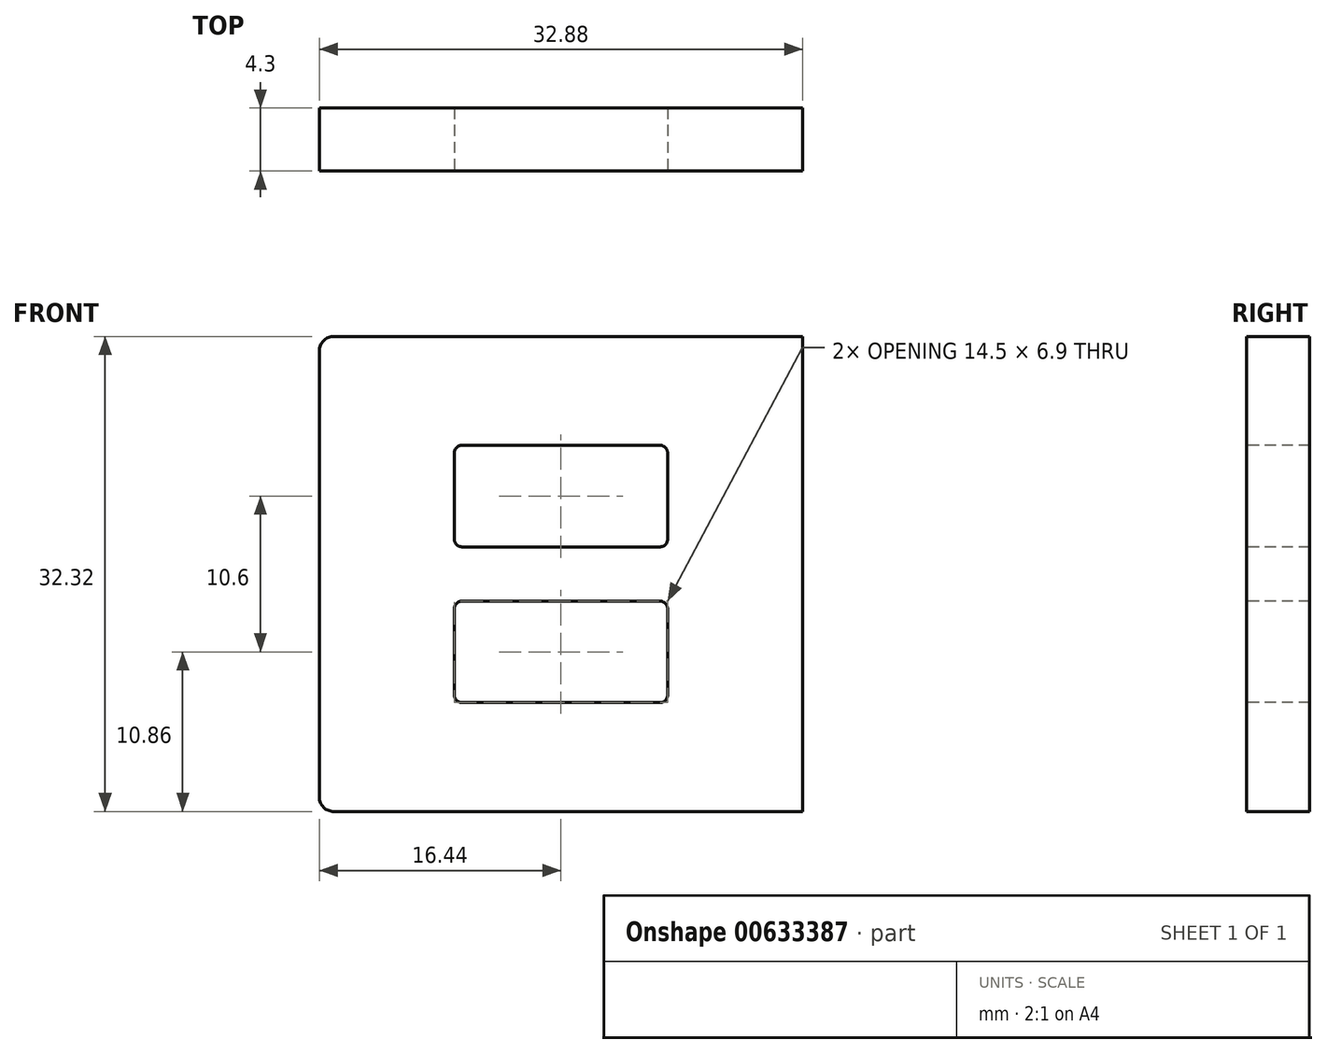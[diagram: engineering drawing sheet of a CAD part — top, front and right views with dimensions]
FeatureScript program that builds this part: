
annotation { "Feature Type Name" : "Feature", "Feature Type Description" : "" }
export const myFeature = defineFeature(function(context is Context, id is Id, definition is map)
    precondition{}
    {
        {
            var Q0;
            Q0=qCreatedBy(makeId("Front.planeOp"),FACE);
            var sketch = newSketch(context, id + "F0", { "sketchPlane" : qUnion([Q0])});
            skLineSegment(sketch, "E0.bottom", {"start": v(16.44, 16.16) * mm, "end": v(-15.44, 16.16) * mm});
            skLineSegment(sketch, "E0.top", {"start": v(16.44, -16.16) * mm, "end": v(-15.44, -16.16) * mm});
            skLineSegment(sketch, "E0.left", {"start": v(16.44, 16.16) * mm, "end": v(16.44, -16.16) * mm});
            skLineSegment(sketch, "E0.right", {"start": v(-16.44, 15.16) * mm, "end": v(-16.44, -15.16) * mm});
            skPoint(sketch, "E0.middle", {"position": v(0, 0) * mm});
            skPoint(sketch, "E1.visualSharp", {"position": v(-16.44, 16.16) * mm});
            skArc(sketch, "E1.filletArc", {"start": v(-15.44, 16.16) * mm, "mid": v(-16.15, 15.87) * mm, "end": v(-16.44, 15.16) * mm});
            skPoint(sketch, "E2.visualSharp", {"position": v(-16.44, -16.16) * mm});
            skArc(sketch, "E2.filletArc", {"start": v(-16.44, -15.16) * mm, "mid": v(-16.15, -15.87) * mm, "end": v(-15.44, -16.16) * mm});
            skSolve(sketch);
        }
        {
            var Q0;
            Q0=makeQuery(id+"F0.imprint","IMPRINT",FACE,{"disambiguationData":[TD([[makeQuery(id+"F0.imprint","IMPRINT",EDGE,{"derivedFrom":sQuery(id+"F0.wireOp",EDGE,"E0.bottom")}),1.0]])]});
            extrude(context, id + "F1", {"entities" : qUnion([Q0]), "depth" : 4.3 * mm, "offsetDistance" : 25 * mm});
        }
        {
            var Q0;
            Q0=makeQuery(id+"F1.opExtrude","CAP_FACE",FACE,{"disambiguationData":[OSD([sQuery(id+"F0.wireOp",EDGE,"E0.bottom"),sQuery(id+"F0.wireOp",EDGE,"E0.top"),sQuery(id+"F0.wireOp",EDGE,"E0.left"),sQuery(id+"F0.wireOp",EDGE,"E0.right"),sQuery(id+"F0.wireOp",EDGE,"E1.filletArc"),sQuery(id+"F0.wireOp",EDGE,"E2.filletArc")])],"isStart":false});
            var sketch = newSketch(context, id + "F2", { "sketchPlane" : qUnion([Q0])});
            skLineSegment(sketch, "E3.bottom", {"start": v(7.25, 8.75) * mm, "end": v(-7.25, 8.75) * mm});
            skLineSegment(sketch, "E3.top", {"start": v(7.25, 1.85) * mm, "end": v(-7.25, 1.85) * mm});
            skLineSegment(sketch, "E3.left", {"start": v(7.25, 8.75) * mm, "end": v(7.25, 1.85) * mm});
            skLineSegment(sketch, "E3.right", {"start": v(-7.25, 8.75) * mm, "end": v(-7.25, 1.85) * mm});
            skPoint(sketch, "E3.middle", {"position": v(0, 5.3) * mm});
            skLineSegment(sketch, "E4.bottom", {"start": v(7.25, -1.85) * mm, "end": v(-7.25, -1.85) * mm});
            skLineSegment(sketch, "E4.top", {"start": v(7.25, -8.75) * mm, "end": v(-7.25, -8.75) * mm});
            skLineSegment(sketch, "E4.left", {"start": v(7.25, -1.85) * mm, "end": v(7.25, -8.75) * mm});
            skLineSegment(sketch, "E4.right", {"start": v(-7.25, -1.85) * mm, "end": v(-7.25, -8.75) * mm});
            skPoint(sketch, "E4.middle", {"position": v(0, -5.3) * mm});
            skSolve(sketch);
        }
        {
            var Q0;
            Q0 = qSketchRegion(id + "F2", true);
            extrude(context, id + "F3", {"entities" : qUnion([Q0]), "operationType" : NewBodyOperationType.REMOVE, "oppositeDirection" : true, "depth" : 25 * mm, "offsetDistance" : 25 * mm});
        }
        {
            var Q0;
            Q0=makeQuery(id+"F3.boolean.opBoolean","COPY",EDGE,{"derivedFrom":makeQuery(id+"F3.opExtrude","SWEPT_EDGE",EDGE,{"disambiguationData":[OSD([sQuery(id+"F2.wireOp",EDGE,"E3.bottom"),sQuery(id+"F2.wireOp",EDGE,"E3.left")])]})});
            var Q1;
            Q1=makeQuery(id+"F3.boolean.opBoolean","COPY",EDGE,{"derivedFrom":makeQuery(id+"F3.opExtrude","SWEPT_EDGE",EDGE,{"disambiguationData":[OSD([sQuery(id+"F2.wireOp",EDGE,"E3.top"),sQuery(id+"F2.wireOp",EDGE,"E3.left")])]})});
            var Q2;
            Q2=makeQuery(id+"F3.boolean.opBoolean","COPY",EDGE,{"derivedFrom":makeQuery(id+"F3.opExtrude","SWEPT_EDGE",EDGE,{"disambiguationData":[OSD([sQuery(id+"F2.wireOp",EDGE,"E3.top"),sQuery(id+"F2.wireOp",EDGE,"E3.right")])]})});
            var Q3;
            Q3=makeQuery(id+"F3.boolean.opBoolean","COPY",EDGE,{"derivedFrom":makeQuery(id+"F3.opExtrude","SWEPT_EDGE",EDGE,{"disambiguationData":[OSD([sQuery(id+"F2.wireOp",EDGE,"E3.bottom"),sQuery(id+"F2.wireOp",EDGE,"E3.right")])]})});
            var Q4;
            Q4=makeQuery(id+"F3.boolean.opBoolean","COPY",EDGE,{"derivedFrom":makeQuery(id+"F3.opExtrude","SWEPT_EDGE",EDGE,{"disambiguationData":[OSD([sQuery(id+"F2.wireOp",EDGE,"E4.bottom"),sQuery(id+"F2.wireOp",EDGE,"E4.right")])]})});
            var Q5;
            Q5=makeQuery(id+"F3.boolean.opBoolean","COPY",EDGE,{"derivedFrom":makeQuery(id+"F3.opExtrude","SWEPT_EDGE",EDGE,{"disambiguationData":[OSD([sQuery(id+"F2.wireOp",EDGE,"E4.bottom"),sQuery(id+"F2.wireOp",EDGE,"E4.left")])]})});
            var Q6;
            Q6=makeQuery(id+"F3.boolean.opBoolean","COPY",EDGE,{"derivedFrom":makeQuery(id+"F3.opExtrude","SWEPT_EDGE",EDGE,{"disambiguationData":[OSD([sQuery(id+"F2.wireOp",EDGE,"E4.top"),sQuery(id+"F2.wireOp",EDGE,"E4.left")])]})});
            var Q7;
            Q7=makeQuery(id+"F3.boolean.opBoolean","COPY",EDGE,{"derivedFrom":makeQuery(id+"F3.opExtrude","SWEPT_EDGE",EDGE,{"disambiguationData":[OSD([sQuery(id+"F2.wireOp",EDGE,"E4.top"),sQuery(id+"F2.wireOp",EDGE,"E4.right")])]})});
            fillet(context, id + "F4", {"entities" : qUnion([Q0, Q1, Q2, Q3, Q4, Q5, Q6, Q7]), "radius" : .5 * mm, "tangentPropagation" : true, "allowEdgeOverflow" : false});
        }
    });
